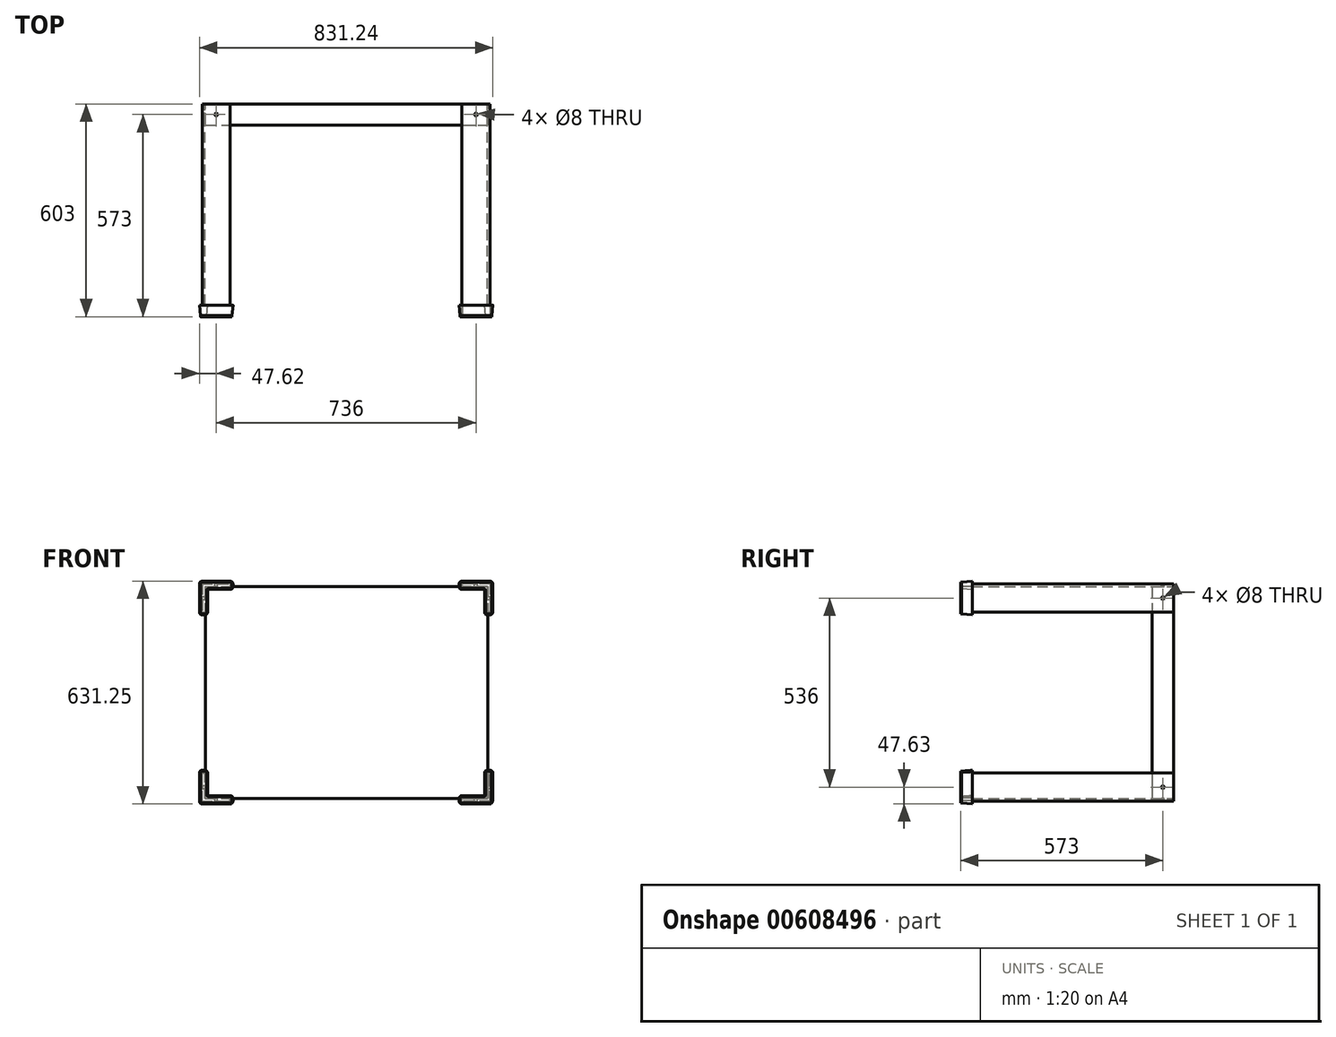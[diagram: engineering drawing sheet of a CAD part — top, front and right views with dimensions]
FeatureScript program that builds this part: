
annotation { "Feature Type Name" : "Feature", "Feature Type Description" : "" }
export const myFeature = defineFeature(function(context is Context, id is Id, definition is map)
    precondition{}
    {
        {
            var Q0;
            Q0=qCreatedBy(makeId("Front.planeOp"),FACE);
            var sketch = newSketch(context, id + "F0", { "sketchPlane" : qUnion([Q0])});
            skLineSegment(sketch, "E0.bottom", {"start": v(-408, 308) * mm, "end": v(-328, 308) * mm});
            skLineSegment(sketch, "E0.top", {"start": v(-408, 228) * mm, "end": v(-400, 228) * mm});
            skLineSegment(sketch, "E0.left", {"start": v(-408, 308) * mm, "end": v(-408, 228) * mm});
            skLineSegment(sketch, "E0.right", {"start": v(-328, 308) * mm, "end": v(-328, 300) * mm});
            skLineSegment(sketch, "E1.bottom", {"start": v(-400, 300) * mm, "end": v(-328, 300) * mm});
            skLineSegment(sketch, "E1.left", {"start": v(-400, 300) * mm, "end": v(-400, 228) * mm});
            skLineSegment(sketch, "E2.bottom", {"start": v(-408, -308) * mm, "end": v(-408, -228) * mm});
            skLineSegment(sketch, "E2.top", {"start": v(-328, -308) * mm, "end": v(-328, -300) * mm});
            skLineSegment(sketch, "E2.left", {"start": v(-408, -308) * mm, "end": v(-328, -308) * mm});
            skLineSegment(sketch, "E2.right", {"start": v(-408, -228) * mm, "end": v(-400, -228) * mm});
            skLineSegment(sketch, "E3.bottom", {"start": v(-400, -300) * mm, "end": v(-400, -228) * mm});
            skLineSegment(sketch, "E3.left", {"start": v(-400, -300) * mm, "end": v(-328, -300) * mm});
            skLineSegment(sketch, "E4.bottom", {"start": v(408, 308) * mm, "end": v(408, 228) * mm});
            skLineSegment(sketch, "E4.top", {"start": v(328, 308) * mm, "end": v(328, 300) * mm});
            skLineSegment(sketch, "E4.left", {"start": v(408, 308) * mm, "end": v(328, 308) * mm});
            skLineSegment(sketch, "E4.right", {"start": v(408, 228) * mm, "end": v(400, 228) * mm});
            skLineSegment(sketch, "E5.bottom", {"start": v(400, 300) * mm, "end": v(400, 228) * mm});
            skLineSegment(sketch, "E5.left", {"start": v(400, 300) * mm, "end": v(328, 300) * mm});
            skLineSegment(sketch, "E6.bottom", {"start": v(408, -308) * mm, "end": v(328, -308) * mm});
            skLineSegment(sketch, "E6.top", {"start": v(408, -228) * mm, "end": v(400, -228) * mm});
            skLineSegment(sketch, "E6.left", {"start": v(408, -308) * mm, "end": v(408, -228) * mm});
            skLineSegment(sketch, "E6.right", {"start": v(328, -308) * mm, "end": v(328, -300) * mm});
            skLineSegment(sketch, "E7.bottom", {"start": v(400, -300) * mm, "end": v(328, -300) * mm});
            skLineSegment(sketch, "E7.left", {"start": v(400, -300) * mm, "end": v(400, -228) * mm});
            skSolve(sketch);
        }
        {
            var Q0;
            Q0=makeQuery(id+"F0.imprint","IMPRINT",FACE,{"disambiguationData":[TD([[makeQuery(id+"F0.imprint","IMPRINT",EDGE,{"derivedFrom":sQuery(id+"F0.wireOp",EDGE,"E2.bottom")}),-1.0]])]});
            var Q1;
            Q1=makeQuery(id+"F0.imprint","IMPRINT",FACE,{"disambiguationData":[TD([[makeQuery(id+"F0.imprint","IMPRINT",EDGE,{"derivedFrom":sQuery(id+"F0.wireOp",EDGE,"E4.bottom")}),-1.0]])]});
            var Q2;
            Q2=makeQuery(id+"F0.imprint","IMPRINT",FACE,{"disambiguationData":[TD([[makeQuery(id+"F0.imprint","IMPRINT",EDGE,{"derivedFrom":sQuery(id+"F0.wireOp",EDGE,"E6.bottom")}),-1.0]])]});
            var Q3;
            Q3=makeQuery(id+"F0.imprint","IMPRINT",FACE,{"disambiguationData":[TD([[makeQuery(id+"F0.imprint","IMPRINT",EDGE,{"derivedFrom":sQuery(id+"F0.wireOp",EDGE,"E0.bottom")}),-1.0]])]});
            extrude(context, id + "F1", {"entities" : qUnion([Q0, Q1, Q2, Q3]), "depth" : 600 * mm, "offsetDistance" : 25 * mm});
        }
        {
            var Q0;
            Q0=makeQuery(id+"F1.opExtrude","SWEPT_FACE",FACE,{"disambiguationData":[OSD([sQuery(id+"F0.wireOp",EDGE,"E0.bottom")])]});
            var sketch = newSketch(context, id + "F2", { "sketchPlane" : qUnion([Q0])});
            skPoint(sketch, "E8", {"position": v(-368, -30) * mm});
            skPoint(sketch, "E9", {"position": v(368, -30) * mm});
            skSolve(sketch);
        }
        {
            var Q0;
            Q0=makeQuery(id+"F1.opExtrude","SWEPT_FACE",FACE,{"disambiguationData":[OSD([sQuery(id+"F0.wireOp",EDGE,"E4.bottom")])]});
            var sketch = newSketch(context, id + "F3", { "sketchPlane" : qUnion([Q0])});
            skPoint(sketch, "E10", {"position": v(-30, 268) * mm});
            skPoint(sketch, "E11", {"position": v(-30, -268) * mm});
            skSolve(sketch);
        }
        {
            var Q0;
            Q0=makeQuery(id+"F1.opExtrude","SWEPT_FACE",FACE,{"disambiguationData":[OSD([sQuery(id+"F0.wireOp",EDGE,"E6.bottom")])]});
            var sketch = newSketch(context, id + "F4", { "sketchPlane" : qUnion([Q0])});
            skPoint(sketch, "E12", {"position": v(368, 30) * mm});
            skPoint(sketch, "E13", {"position": v(-368, 30) * mm});
            skSolve(sketch);
        }
        {
            var Q0;
            Q0=makeQuery(id+"F1.opExtrude","SWEPT_FACE",FACE,{"disambiguationData":[OSD([sQuery(id+"F0.wireOp",EDGE,"E2.bottom")])]});
            var sketch = newSketch(context, id + "F5", { "sketchPlane" : qUnion([Q0])});
            skPoint(sketch, "E14", {"position": v(30, -268) * mm});
            skPoint(sketch, "E15", {"position": v(30, 268) * mm});
            skSolve(sketch);
        }
        {
            var Q0;
            Q0=sQuery(id+"F3.wireOp",VERTEX,"E11");
            var Q1;
            Q1=sQuery(id+"F3.wireOp",VERTEX,"E10");
            var Q2;
            Q2=sQuery(id+"F2.wireOp",VERTEX,"E8");
            var Q3;
            Q3=sQuery(id+"F2.wireOp",VERTEX,"E9");
            var Q4;
            Q4=sQuery(id+"F4.wireOp",VERTEX,"E12");
            var Q5;
            Q5=sQuery(id+"F4.wireOp",VERTEX,"E13");
            var Q6;
            Q6=sQuery(id+"F5.wireOp",VERTEX,"E14");
            var Q7;
            Q7=sQuery(id+"F5.wireOp",VERTEX,"E15");
            var Q8;
            Q8=makeQuery(id+"F1.opExtrude","SWEPT_BODY",BODY,{"disambiguationData":[OSD([sQuery(id+"F0.wireOp",EDGE,"E2.bottom"),sQuery(id+"F0.wireOp",EDGE,"E2.top"),sQuery(id+"F0.wireOp",EDGE,"E2.left"),sQuery(id+"F0.wireOp",EDGE,"E2.right"),sQuery(id+"F0.wireOp",EDGE,"E3.bottom"),sQuery(id+"F0.wireOp",EDGE,"E3.left")])]});
            var Q9;
            Q9=makeQuery(id+"F1.opExtrude","SWEPT_BODY",BODY,{"disambiguationData":[OSD([sQuery(id+"F0.wireOp",EDGE,"E6.bottom"),sQuery(id+"F0.wireOp",EDGE,"E6.top"),sQuery(id+"F0.wireOp",EDGE,"E6.left"),sQuery(id+"F0.wireOp",EDGE,"E6.right"),sQuery(id+"F0.wireOp",EDGE,"E7.bottom"),sQuery(id+"F0.wireOp",EDGE,"E7.left")])]});
            var Q10;
            Q10=makeQuery(id+"F1.opExtrude","SWEPT_BODY",BODY,{"disambiguationData":[OSD([sQuery(id+"F0.wireOp",EDGE,"E0.bottom"),sQuery(id+"F0.wireOp",EDGE,"E0.top"),sQuery(id+"F0.wireOp",EDGE,"E0.left"),sQuery(id+"F0.wireOp",EDGE,"E0.right"),sQuery(id+"F0.wireOp",EDGE,"E1.bottom"),sQuery(id+"F0.wireOp",EDGE,"E1.left")])]});
            var Q11;
            Q11=makeQuery(id+"F1.opExtrude","SWEPT_BODY",BODY,{"disambiguationData":[OSD([sQuery(id+"F0.wireOp",EDGE,"E4.bottom"),sQuery(id+"F0.wireOp",EDGE,"E4.top"),sQuery(id+"F0.wireOp",EDGE,"E4.left"),sQuery(id+"F0.wireOp",EDGE,"E4.right"),sQuery(id+"F0.wireOp",EDGE,"E5.bottom"),sQuery(id+"F0.wireOp",EDGE,"E5.left")])]});
            hole(context, id + "F6", {"style" : HoleStyle.SIMPLE, "endStyle" : HoleEndStyle.THROUGH, "standardTappedOrClearance" : lookupTablePath({ "standard" : "ISO", "size" : "8", "type" : "Drilled" }), "standardBlindInLast" : lookupTablePath({ "standard" : "ISO", "size" : "8", "type" : "Drilled" }), "holeDiameter" : 8 * mm, "majorDiameter" : 6 * mm, "isTappedThrough" : true, "tappedDepth" : 12 * mm, "tapClearance" : 3, "startFromSketch" : true, "locations" : qUnion([Q0, Q1, Q2, Q3, Q4, Q5, Q6, Q7]), "scope" : qUnion([Q8, Q9, Q10, Q11])});
        }
        {
            var Q0;
            Q0=makeQuery(id+"F1.opExtrude","CAP_FACE",FACE,{"disambiguationData":[OSD([sQuery(id+"F0.wireOp",EDGE,"E6.bottom"),sQuery(id+"F0.wireOp",EDGE,"E6.top"),sQuery(id+"F0.wireOp",EDGE,"E6.left"),sQuery(id+"F0.wireOp",EDGE,"E6.right"),sQuery(id+"F0.wireOp",EDGE,"E7.bottom"),sQuery(id+"F0.wireOp",EDGE,"E7.left")])],"isStart":false});
            var sketch = newSketch(context, id + "F7", { "sketchPlane" : qUnion([Q0])});
            skLineSegment(sketch, "E16", {"start": v(-328, 313) * mm, "end": v(-408, 313) * mm});
            skLineSegment(sketch, "E17", {"start": v(-413, 308) * mm, "end": v(-413, 228) * mm});
            skLineSegment(sketch, "E18", {"start": v(-408, 223) * mm, "end": v(-400, 223) * mm});
            skLineSegment(sketch, "E19", {"start": v(-395, 228) * mm, "end": v(-395, 290) * mm});
            skLineSegment(sketch, "E20", {"start": v(-390, 295) * mm, "end": v(-328, 295) * mm});
            skLineSegment(sketch, "E21", {"start": v(-323, 300) * mm, "end": v(-323, 308) * mm});
            skPoint(sketch, "E22.visualSharp", {"position": v(-323, 313) * mm});
            skArc(sketch, "E22.filletArc", {"start": v(-323, 308) * mm, "mid": v(-324.46, 311.54) * mm, "end": v(-328, 313) * mm});
            skPoint(sketch, "E23.visualSharp", {"position": v(-323, 295) * mm});
            skArc(sketch, "E23.filletArc", {"start": v(-328, 295) * mm, "mid": v(-324.46, 296.46) * mm, "end": v(-323, 300) * mm});
            skPoint(sketch, "E24.visualSharp", {"position": v(-413, 313) * mm});
            skArc(sketch, "E24.filletArc", {"start": v(-408, 313) * mm, "mid": v(-411.54, 311.54) * mm, "end": v(-413, 308) * mm});
            skPoint(sketch, "E25.visualSharp", {"position": v(-395, 295) * mm});
            skArc(sketch, "E25.filletArc", {"start": v(-390, 295) * mm, "mid": v(-393.54, 293.54) * mm, "end": v(-395, 290) * mm});
            skPoint(sketch, "E26.visualSharp", {"position": v(-395, 223) * mm});
            skArc(sketch, "E26.filletArc", {"start": v(-400, 223) * mm, "mid": v(-396.46, 224.46) * mm, "end": v(-395, 228) * mm});
            skPoint(sketch, "E27.visualSharp", {"position": v(-413, 223) * mm});
            skArc(sketch, "E27.filletArc", {"start": v(-413, 228) * mm, "mid": v(-411.54, 224.46) * mm, "end": v(-408, 223) * mm});
            skLineSegment(sketch, "E28", {"start": v(413, 228) * mm, "end": v(413, 308) * mm});
            skLineSegment(sketch, "E29", {"start": v(408, 313) * mm, "end": v(328, 313) * mm});
            skLineSegment(sketch, "E30", {"start": v(328, 295) * mm, "end": v(390, 295) * mm});
            skLineSegment(sketch, "E31", {"start": v(395, 290) * mm, "end": v(395, 228) * mm});
            skLineSegment(sketch, "E32", {"start": v(400, 223) * mm, "end": v(408, 223) * mm});
            skPoint(sketch, "E33.visualSharp", {"position": v(413, 223) * mm});
            skArc(sketch, "E33.filletArc", {"start": v(408, 223) * mm, "mid": v(411.54, 224.46) * mm, "end": v(413, 228) * mm});
            skPoint(sketch, "E34.visualSharp", {"position": v(413, 313) * mm});
            skArc(sketch, "E34.filletArc", {"start": v(413, 308) * mm, "mid": v(411.54, 311.54) * mm, "end": v(408, 313) * mm});
            skPoint(sketch, "E35.visualSharp", {"position": v(395, 295) * mm});
            skArc(sketch, "E35.filletArc", {"start": v(395, 290) * mm, "mid": v(393.54, 293.54) * mm, "end": v(390, 295) * mm});
            skPoint(sketch, "E36.visualSharp", {"position": v(328, 295) * mm});
            skArc(sketch, "E36.filletArc", {"start": v(323, 299.95) * mm, "mid": v(324.48, 296.45) * mm, "end": v(328, 295) * mm});
            skPoint(sketch, "E37.visualSharp", {"position": v(328, 313) * mm});
            skArc(sketch, "E37.filletArc", {"start": v(328, 313) * mm, "mid": v(324.46, 311.54) * mm, "end": v(323, 308) * mm});
            skLineSegment(sketch, "E38", {"start": v(323, 308) * mm, "end": v(323, 299.95) * mm});
            skPoint(sketch, "E39.visualSharp", {"position": v(395, 223) * mm});
            skArc(sketch, "E39.filletArc", {"start": v(395, 228) * mm, "mid": v(396.46, 224.46) * mm, "end": v(400, 223) * mm});
            skLineSegment(sketch, "E40", {"start": v(329.07, -312.86) * mm, "end": v(407.28, -312.86) * mm});
            skLineSegment(sketch, "E41", {"start": v(412.28, -307.86) * mm, "end": v(412.28, -225.25) * mm});
            skLineSegment(sketch, "E42", {"start": v(408, -223) * mm, "end": v(400, -223) * mm});
            skLineSegment(sketch, "E43", {"start": v(395, -228) * mm, "end": v(395, -290) * mm});
            skLineSegment(sketch, "E44", {"start": v(390, -295) * mm, "end": v(328, -295) * mm});
            skLineSegment(sketch, "E45", {"start": v(323, -299) * mm, "end": v(323, -307) * mm});
            skPoint(sketch, "E46.visualSharp", {"position": v(323, -312) * mm});
            skArc(sketch, "E46.filletArc", {"start": v(323, -307) * mm, "mid": v(324.42, -311.6) * mm, "end": v(329.07, -312.86) * mm});
            skPoint(sketch, "E47.visualSharp", {"position": v(323, -294) * mm});
            skArc(sketch, "E47.filletArc", {"start": v(328, -295) * mm, "mid": v(324.78, -296.1) * mm, "end": v(323, -299) * mm});
            skPoint(sketch, "E48.visualSharp", {"position": v(395, -222) * mm});
            skArc(sketch, "E48.filletArc", {"start": v(400, -223) * mm, "mid": v(396.46, -224.46) * mm, "end": v(395, -228) * mm});
            skPoint(sketch, "E49.visualSharp", {"position": v(413, -222) * mm});
            skArc(sketch, "E49.filletArc", {"start": v(412.28, -225.25) * mm, "mid": v(410.43, -223.57) * mm, "end": v(408, -223) * mm});
            skPoint(sketch, "E50.visualSharp", {"position": v(395, -295) * mm});
            skArc(sketch, "E50.filletArc", {"start": v(390, -295) * mm, "mid": v(393.54, -293.54) * mm, "end": v(395, -290) * mm});
            skPoint(sketch, "E51.visualSharp", {"position": v(412.28, -312.86) * mm});
            skArc(sketch, "E51.filletArc", {"start": v(407.28, -312.86) * mm, "mid": v(410.81, -311.4) * mm, "end": v(412.28, -307.86) * mm});
            skLineSegment(sketch, "E52", {"start": v(-413, -227.86) * mm, "end": v(-413, -307.86) * mm});
            skLineSegment(sketch, "E53", {"start": v(-408, -312.86) * mm, "end": v(-328, -312.86) * mm});
            skLineSegment(sketch, "E54", {"start": v(-323, -307.86) * mm, "end": v(-323, -299.86) * mm});
            skLineSegment(sketch, "E55", {"start": v(-328, -294.86) * mm, "end": v(-390, -294.86) * mm});
            skLineSegment(sketch, "E56", {"start": v(-395, -289.86) * mm, "end": v(-395, -227.86) * mm});
            skLineSegment(sketch, "E57", {"start": v(-400, -222.86) * mm, "end": v(-408, -222.86) * mm});
            skPoint(sketch, "E58.visualSharp", {"position": v(-413, -222.86) * mm});
            skArc(sketch, "E58.filletArc", {"start": v(-408, -222.86) * mm, "mid": v(-411.54, -224.33) * mm, "end": v(-413, -227.86) * mm});
            skPoint(sketch, "E59.visualSharp", {"position": v(-395, -222.86) * mm});
            skArc(sketch, "E59.filletArc", {"start": v(-395, -227.86) * mm, "mid": v(-396.46, -224.33) * mm, "end": v(-400, -222.86) * mm});
            skPoint(sketch, "E60.visualSharp", {"position": v(-413, -312.86) * mm});
            skArc(sketch, "E60.filletArc", {"start": v(-413, -307.86) * mm, "mid": v(-411.54, -311.4) * mm, "end": v(-408, -312.86) * mm});
            skPoint(sketch, "E61.visualSharp", {"position": v(-395, -294.86) * mm});
            skArc(sketch, "E61.filletArc", {"start": v(-395, -289.86) * mm, "mid": v(-393.54, -293.4) * mm, "end": v(-390, -294.86) * mm});
            skPoint(sketch, "E62.visualSharp", {"position": v(-323, -294.86) * mm});
            skArc(sketch, "E62.filletArc", {"start": v(-323, -299.86) * mm, "mid": v(-324.46, -296.33) * mm, "end": v(-328, -294.86) * mm});
            skPoint(sketch, "E63.visualSharp", {"position": v(-323, -312.86) * mm});
            skArc(sketch, "E63.filletArc", {"start": v(-328, -312.86) * mm, "mid": v(-324.46, -311.4) * mm, "end": v(-323, -307.86) * mm});
            skSolve(sketch);
        }
        {
            var Q0;
            Q0=makeQuery(id+"F7.imprint","IMPRINT",FACE,{"disambiguationData":[TD([[makeQuery(id+"F7.imprint","IMPRINT",EDGE,{"derivedFrom":sQuery(id+"F7.wireOp",EDGE,"E28")}),1.0]])]});
            var Q1;
            Q1=makeQuery(id+"F7.imprint","IMPRINT",FACE,{"disambiguationData":[TD([[makeQuery(id+"F7.imprint","IMPRINT",EDGE,{"derivedFrom":sQuery(id+"F7.wireOp",EDGE,"E52")}),1.0]])]});
            var Q2;
            Q2=makeQuery(id+"F7.imprint","IMPRINT",FACE,{"disambiguationData":[TD([[makeQuery(id+"F7.imprint","IMPRINT",EDGE,{"derivedFrom":sQuery(id+"F7.wireOp",EDGE,"E16")}),1.0]])]});
            var Q3;
            Q3=makeQuery(id+"F7.imprint","IMPRINT",FACE,{"disambiguationData":[TD([[makeQuery(id+"F7.imprint","IMPRINT",EDGE,{"derivedFrom":makeQuery(id+"F1.opExtrude","CAP_EDGE",EDGE,{"disambiguationData":[OSD([sQuery(id+"F0.wireOp",EDGE,"E6.bottom")])],"isStart":false})}),-1.0]])]});
            var Q4;
            Q4=makeQuery(id+"F7.imprint","IMPRINT",FACE,{"disambiguationData":[TD([[makeQuery(id+"F7.imprint","IMPRINT",EDGE,{"derivedFrom":sQuery(id+"F7.wireOp",EDGE,"E40")}),1.0]])]});
            var Q5;
            Q5=makeQuery(id+"F1.opExtrude","CAP_FACE",FACE,{"disambiguationData":[OSD([sQuery(id+"F0.wireOp",EDGE,"E6.bottom"),sQuery(id+"F0.wireOp",EDGE,"E6.top"),sQuery(id+"F0.wireOp",EDGE,"E6.left"),sQuery(id+"F0.wireOp",EDGE,"E6.right"),sQuery(id+"F0.wireOp",EDGE,"E7.bottom"),sQuery(id+"F0.wireOp",EDGE,"E7.left")])],"isStart":false});
            extrude(context, id + "F8", {"entities" : qUnion([Q0, Q1, Q2, Q3, Q4, Q5]), "operationType" : NewBodyOperationType.ADD, "depth" : -30 * mm, "offsetDistance" : 25 * mm, "hasDraft" : true, "draftAngle" : 5 * degree, "hasSecondDirection" : true, "secondDirectionOppositeDirection" : true, "secondDirectionDepth" : -3 * mm});
        }
        {
            var Q0;
            Q0=qCreatedBy(makeId("Front.planeOp"),FACE);
            var sketch = newSketch(context, id + "F9", { "sketchPlane" : qUnion([Q0])});
            skLineSegment(sketch, "E64.bottom", {"start": v(-398.7, 300) * mm, "end": v(401.3, 300) * mm});
            skLineSegment(sketch, "E64.top", {"start": v(-398.7, -300) * mm, "end": v(401.3, -300) * mm});
            skLineSegment(sketch, "E64.left", {"start": v(-398.7, 300) * mm, "end": v(-398.7, -300) * mm});
            skLineSegment(sketch, "E64.right", {"start": v(401.3, 300) * mm, "end": v(401.3, -300) * mm});
            skPoint(sketch, "E65", {"position": v(0, 0) * mm});
            skPoint(sketch, "E65.positionSnap0", {"position": v(-398.7, 0) * mm});
            skSolve(sketch);
        }
        {
            var Q0;
            Q0=makeQuery(id+"F9.imprint","IMPRINT",FACE,{"disambiguationData":[TD([[makeQuery(id+"F9.imprint","IMPRINT",EDGE,{"derivedFrom":sQuery(id+"F9.wireOp",EDGE,"E64.bottom")}),-1.0]])]});
            extrude(context, id + "F10", {"entities" : qUnion([Q0]), "depth" : 60 * mm, "offsetDistance" : 25 * mm});
        }
    });
